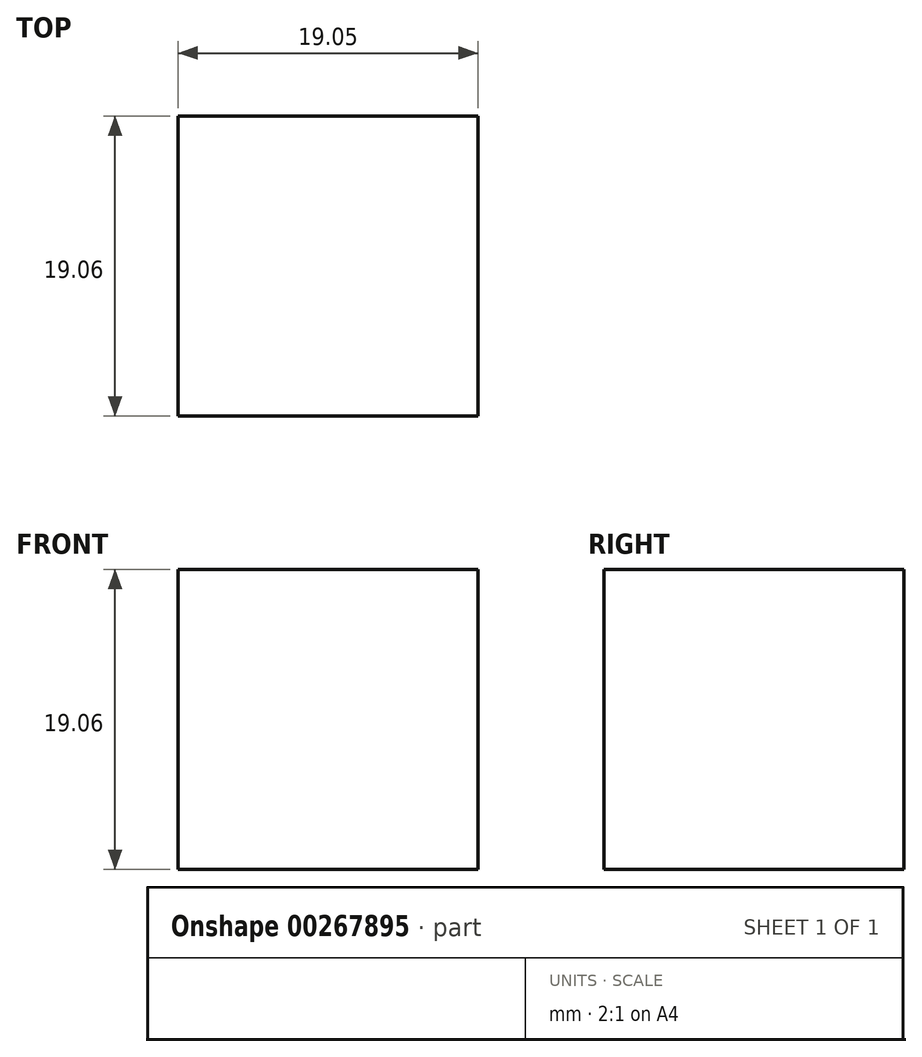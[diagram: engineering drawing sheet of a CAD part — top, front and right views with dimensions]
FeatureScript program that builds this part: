
annotation { "Feature Type Name" : "Feature", "Feature Type Description" : "" }
export const myFeature = defineFeature(function(context is Context, id is Id, definition is map)
    precondition{}
    {
        {
            var Q0;
            Q0=qCreatedBy(makeId("Front.planeOp"),FACE);
            var sketch = newSketch(context, id + "F0", { "sketchPlane" : qUnion([Q0])});
            skLineSegment(sketch, "E0.bottom", {"start": v(-14.44, 9.53) * mm, "end": v(4.6, 9.53) * mm});
            skLineSegment(sketch, "E0.top", {"start": v(-14.44, -9.52) * mm, "end": v(4.6, -9.52) * mm});
            skLineSegment(sketch, "E0.left", {"start": v(-14.44, 9.53) * mm, "end": v(-14.44, -9.53) * mm});
            skLineSegment(sketch, "E0.right", {"start": v(4.6, 9.53) * mm, "end": v(4.6, -9.53) * mm});
            skPoint(sketch, "E0.middle", {"position": v(-4.92, 0) * mm});
            skSolve(sketch);
        }
        {
            var Q0;
            Q0=makeQuery(id+"F0.imprint","IMPRINT",FACE,{"disambiguationData":[TD([[makeQuery(id+"F0.imprint","IMPRINT",EDGE,{"derivedFrom":sQuery(id+"F0.wireOp",EDGE,"E0.bottom")}),-1.0]])]});
            extrude(context, id + "F1", {"entities" : qUnion([Q0]), "endBound" : BoundingType.SYMMETRIC, "depth" : 19.05 * mm});
        }
    });
